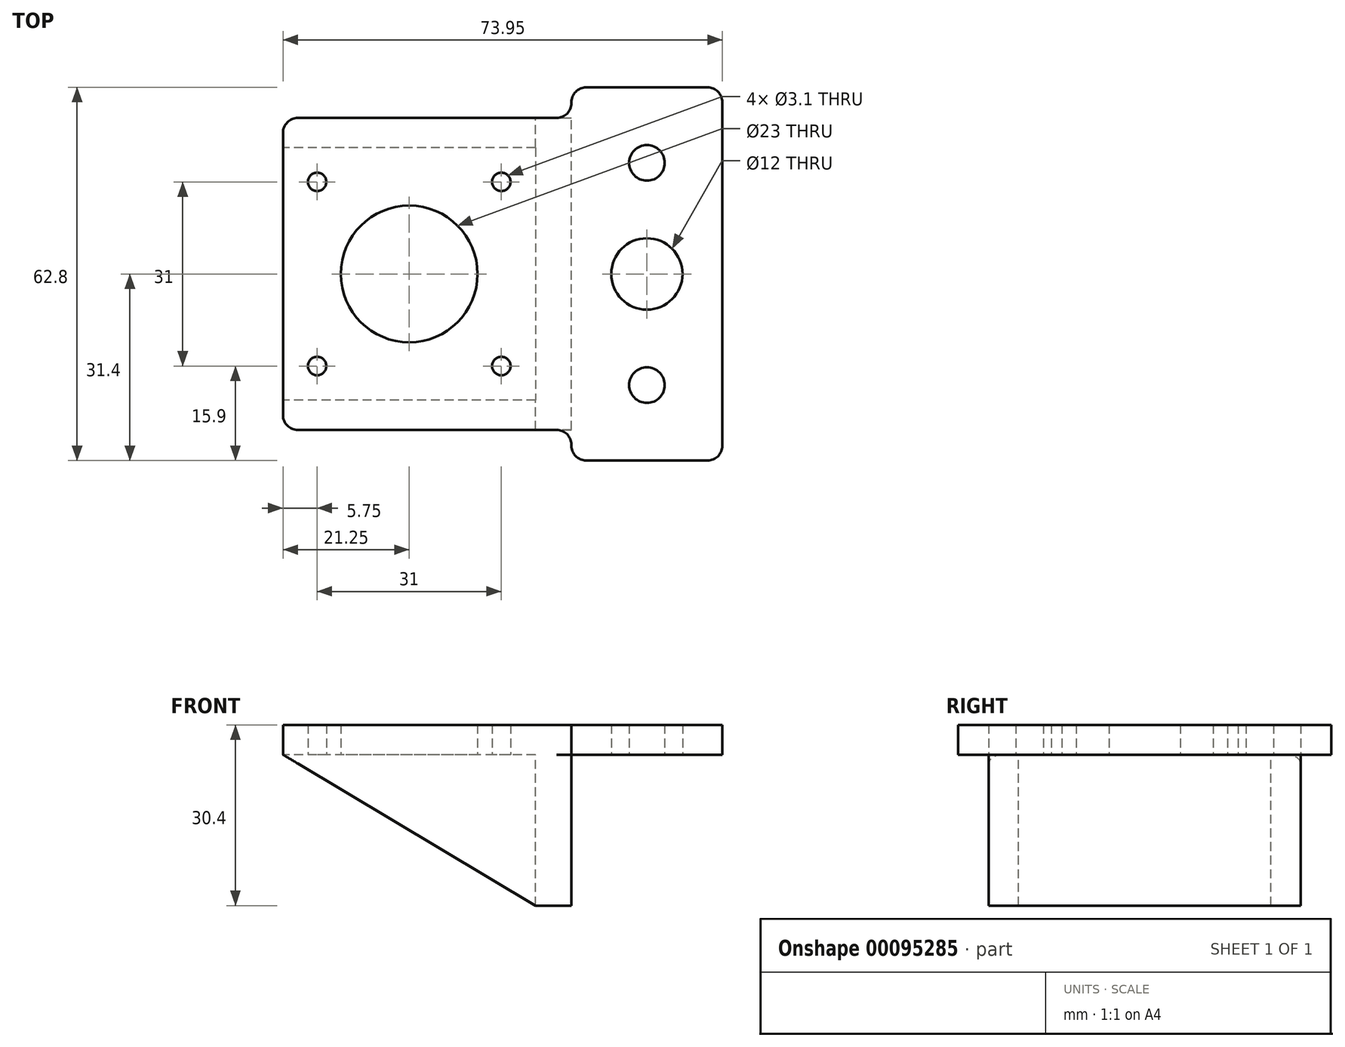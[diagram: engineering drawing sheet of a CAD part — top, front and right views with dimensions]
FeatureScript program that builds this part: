
annotation { "Feature Type Name" : "Feature", "Feature Type Description" : "" }
export const myFeature = defineFeature(function(context is Context, id is Id, definition is map)
    precondition{}
    {
        {
            var Q0;
            Q0=qCreatedBy(makeId("Top.planeOp"),FACE);
            var sketch = newSketch(context, id + "F0", { "sketchPlane" : qUnion([Q0])});
            skLineSegment(sketch, "E0.bottom", {"start": v(21.25, 21.25) * mm, "end": v(-21.25, 21.25) * mm});
            skLineSegment(sketch, "E0.top", {"start": v(21.25, -21.25) * mm, "end": v(-21.25, -21.25) * mm});
            skLineSegment(sketch, "E0.left", {"start": v(21.25, 21.25) * mm, "end": v(21.25, -21.25) * mm});
            skLineSegment(sketch, "E0.right", {"start": v(-21.25, 21.25) * mm, "end": v(-21.25, -21.25) * mm});
            skPoint(sketch, "E0.middle", {"position": v(0, 0) * mm});
            skCircle(sketch, "E1", {"center": v(-15.5, 15.5) * mm, "radius": 1.55 * mm});
            skCircle(sketch, "E2.MirrorC", {"center": v(15.5, 15.5) * mm, "radius": 1.55 * mm});
            skCircle(sketch, "E3.MirrorC", {"center": v(-15.5, -15.5) * mm, "radius": 1.55 * mm});
            skCircle(sketch, "E4.MirrorC", {"center": v(15.5, -15.5) * mm, "radius": 1.55 * mm});
            skLineSegment(sketch, "E5.bottom", {"start": v(21.25, 21.25) * mm, "end": v(27.3, 21.25) * mm});
            skLineSegment(sketch, "E5.top", {"start": v(21.25, -21.25) * mm, "end": v(27.3, -21.25) * mm});
            skLineSegment(sketch, "E5.right", {"start": v(27.3, 21.25) * mm, "end": v(27.3, -21.25) * mm});
            skLineSegment(sketch, "E6.bottom", {"start": v(27.3, -31.4) * mm, "end": v(52.7, -31.4) * mm});
            skLineSegment(sketch, "E6.top", {"start": v(27.3, 31.4) * mm, "end": v(52.7, 31.4) * mm});
            skLineSegment(sketch, "E6.left", {"start": v(27.3, -31.4) * mm, "end": v(27.3, 31.4) * mm});
            skLineSegment(sketch, "E6.right", {"start": v(52.7, -31.4) * mm, "end": v(52.7, 31.4) * mm});
            skPoint(sketch, "E7", {"position": v(52.7, 0) * mm});
            skLineSegment(sketch, "E8.bottom", {"start": v(-21.25, 21.25) * mm, "end": v(27.3, 21.25) * mm});
            skLineSegment(sketch, "E8.top", {"start": v(-21.25, 26.25) * mm, "end": v(27.3, 26.25) * mm});
            skLineSegment(sketch, "E8.left", {"start": v(-21.25, 21.25) * mm, "end": v(-21.25, 26.25) * mm});
            skLineSegment(sketch, "E8.right", {"start": v(27.3, 21.25) * mm, "end": v(27.3, 26.25) * mm});
            skLineSegment(sketch, "E9.bottom", {"start": v(-21.25, -21.25) * mm, "end": v(27.3, -21.25) * mm});
            skLineSegment(sketch, "E9.top", {"start": v(-21.25, -26.25) * mm, "end": v(27.3, -26.25) * mm});
            skLineSegment(sketch, "E9.left", {"start": v(-21.25, -21.25) * mm, "end": v(-21.25, -26.25) * mm});
            skLineSegment(sketch, "E9.right", {"start": v(27.3, -21.25) * mm, "end": v(27.3, -26.25) * mm});
            skCircle(sketch, "E10", {"center": v(40, 0) * mm, "radius": 6 * mm});
            skPoint(sketch, "E10.centerSnap0", {"position": v(40, 31.4) * mm});
            skCircle(sketch, "E11", {"center": v(40, 18.7) * mm, "radius": 3 * mm});
            skCircle(sketch, "E12.MirrorC", {"center": v(40, -18.7) * mm, "radius": 3 * mm});
            skCircle(sketch, "E13", {"center": v(0, 0) * mm, "radius": 11.5 * mm});
            skSolve(sketch);
        }
        {
            var Q0;
            {var subQ0=sQuery(id+"F0.wireOp",EDGE,"E0.right");Q0=makeQuery(id+"F0.imprint","IMPRINT",FACE,{"disambiguationData":[TD([[makeQuery(id+"F0.imprint","IMPRINT",EDGE,{"derivedFrom":subQ0}),1.0]])]});}
            var Q1;
            Q1=makeQuery(id+"F0.imprint","IMPRINT",FACE,{"disambiguationData":[TD([[makeQuery(id+"F0.imprint","IMPRINT",EDGE,{"derivedFrom":sQuery(id+"F0.wireOp",EDGE,"E8.top")}),-1.0]])]});
            var Q2;
            {var subQ0=sQuery(id+"F0.wireOp",EDGE,"E0.left");Q2=makeQuery(id+"F0.imprint","IMPRINT",FACE,{"disambiguationData":[TD([[makeQuery(id+"F0.imprint","IMPRINT",EDGE,{"derivedFrom":subQ0}),1.0]])]});}
            var Q3;
            Q3=makeQuery(id+"F0.imprint","IMPRINT",FACE,{"disambiguationData":[TD([[makeQuery(id+"F0.imprint","IMPRINT",EDGE,{"derivedFrom":sQuery(id+"F0.wireOp",EDGE,"E9.top")}),1.0]])]});
            var Q4;
            {var subQ4=sQuery(id+"F0.wireOp",EDGE,"E6.bottom");Q4=makeQuery(id+"F0.imprint","IMPRINT",FACE,{"disambiguationData":[TD([[makeQuery(id+"F0.imprint","IMPRINT",EDGE,{"derivedFrom":subQ4}),1.0]])]});}
            extrude(context, id + "F1", {"entities" : qUnion([Q0, Q1, Q2, Q3, Q4]), "depth" : 5 * mm});
        }
        {
            var Q0;
            Q0=makeQuery(id+"F0.imprint","IMPRINT",FACE,{"disambiguationData":[TD([[makeQuery(id+"F0.imprint","IMPRINT",EDGE,{"derivedFrom":sQuery(id+"F0.wireOp",EDGE,"E9.top")}),1.0]])]});
            var Q1;
            {var subQ0=sQuery(id+"F0.wireOp",EDGE,"E0.left");Q1=makeQuery(id+"F0.imprint","IMPRINT",FACE,{"disambiguationData":[TD([[makeQuery(id+"F0.imprint","IMPRINT",EDGE,{"derivedFrom":subQ0}),1.0]])]});}
            var Q2;
            Q2=makeQuery(id+"F0.imprint","IMPRINT",FACE,{"disambiguationData":[TD([[makeQuery(id+"F0.imprint","IMPRINT",EDGE,{"derivedFrom":sQuery(id+"F0.wireOp",EDGE,"E8.top")}),-1.0]])]});
            extrude(context, id + "F2", {"entities" : qUnion([Q0, Q1, Q2]), "operationType" : NewBodyOperationType.ADD, "oppositeDirection" : true, "depth" : 25.4 * mm});
        }
        {
            var Q0;
            Q0=makeQuery(id+"F2.opExtrude","CAP_EDGE",EDGE,{"disambiguationData":[OSD([sQuery(id+"F0.wireOp",EDGE,"E9.left")])],"isStart":false});
            var Q1;
            Q1=makeQuery(id+"F2.opExtrude","CAP_EDGE",EDGE,{"disambiguationData":[OSD([sQuery(id+"F0.wireOp",EDGE,"E8.left")])],"isStart":false});
            chamfer(context, id + "F3", {"entities" : qUnion([Q0, Q1]), "chamferType" : ChamferType.TWO_OFFSETS, "width1" : 25.4 * mm, "oppositeDirection" : false, "width2" : 42.5 * mm, "tangentPropagation" : true});
        }
        {
            var Q0;
            Q0=makeQuery(id+"F1.opExtrude","SWEPT_EDGE",EDGE,{"disambiguationData":[OSD([sQuery(id+"F0.wireOp",EDGE,"E6.top"),sQuery(id+"F0.wireOp",EDGE,"E6.left")])]});
            var Q1;
            Q1=makeQuery(id+"F1.opExtrude","SWEPT_EDGE",EDGE,{"disambiguationData":[OSD([sQuery(id+"F0.wireOp",EDGE,"E6.top"),sQuery(id+"F0.wireOp",EDGE,"E6.right")])]});
            var Q2;
            Q2=makeQuery(id+"F1.opExtrude","SWEPT_EDGE",EDGE,{"disambiguationData":[OSD([sQuery(id+"F0.wireOp",EDGE,"E6.left"),sQuery(id+"F0.wireOp",EDGE,"E8.top"),sQuery(id+"F0.wireOp",EDGE,"E8.right")])]});
            var Q3;
            {var subQ0=sQuery(id+"F0.wireOp",EDGE,"E8.left");var subQ1=sQuery(id+"F0.wireOp",EDGE,"E8.top");Q3=makeQuery(id+"F2.boolean.opBoolean","MERGE",EDGE,{"derivedFrom":[makeQuery(id+"F1.opExtrude","SWEPT_EDGE",EDGE,{"disambiguationData":[OSD([subQ1,subQ0])]}),makeQuery(id+"F2.opExtrude","SWEPT_EDGE",EDGE,{"disambiguationData":[OSD([subQ1,subQ0])]})]});}
            var Q4;
            Q4=makeQuery(id+"F1.opExtrude","SWEPT_EDGE",EDGE,{"disambiguationData":[OSD([sQuery(id+"F0.wireOp",EDGE,"E6.bottom"),sQuery(id+"F0.wireOp",EDGE,"E6.right")])]});
            var Q5;
            Q5=makeQuery(id+"F1.opExtrude","SWEPT_EDGE",EDGE,{"disambiguationData":[OSD([sQuery(id+"F0.wireOp",EDGE,"E6.bottom"),sQuery(id+"F0.wireOp",EDGE,"E6.left")])]});
            var Q6;
            Q6=makeQuery(id+"F1.opExtrude","SWEPT_EDGE",EDGE,{"disambiguationData":[OSD([sQuery(id+"F0.wireOp",EDGE,"E6.left"),sQuery(id+"F0.wireOp",EDGE,"E9.top"),sQuery(id+"F0.wireOp",EDGE,"E9.right")])]});
            var Q7;
            {var subQ0=sQuery(id+"F0.wireOp",EDGE,"E9.left");var subQ1=sQuery(id+"F0.wireOp",EDGE,"E9.top");Q7=makeQuery(id+"F2.boolean.opBoolean","MERGE",EDGE,{"derivedFrom":[makeQuery(id+"F1.opExtrude","SWEPT_EDGE",EDGE,{"disambiguationData":[OSD([subQ1,subQ0])]}),makeQuery(id+"F2.opExtrude","SWEPT_EDGE",EDGE,{"disambiguationData":[OSD([subQ1,subQ0])]})]});}
            fillet(context, id + "F4", {"entities" : qUnion([Q0, Q1, Q2, Q3, Q4, Q5, Q6, Q7]), "radius" : 2.5 * mm, "tangentPropagation" : true, "allowEdgeOverflow" : false});
        }
    });
